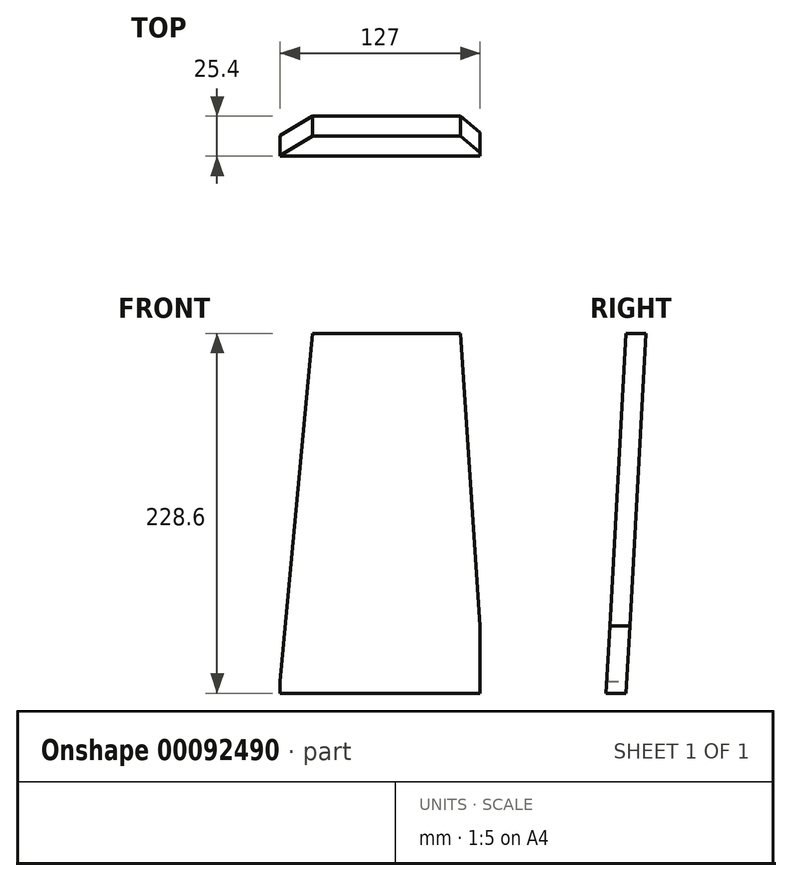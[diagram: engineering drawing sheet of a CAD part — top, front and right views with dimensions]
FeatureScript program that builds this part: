
annotation { "Feature Type Name" : "Feature", "Feature Type Description" : "" }
export const myFeature = defineFeature(function(context is Context, id is Id, definition is map)
    precondition{}
    {
        {
            var Q0;
            Q0=qCreatedBy(makeId("Top.planeOp"),FACE);
            var sketch = newSketch(context, id + "F0", { "sketchPlane" : qUnion([Q0])});
            skLineSegment(sketch, "E0.bottom", {"start": v(63.5, 6.35) * mm, "end": v(-63.5, 6.35) * mm});
            skLineSegment(sketch, "E0.top", {"start": v(63.5, -6.35) * mm, "end": v(-63.5, -6.35) * mm});
            skLineSegment(sketch, "E0.left", {"start": v(63.5, 6.35) * mm, "end": v(63.5, -6.35) * mm});
            skLineSegment(sketch, "E0.right", {"start": v(-63.5, 6.35) * mm, "end": v(-63.5, -6.35) * mm});
            skPoint(sketch, "E0.middle", {"position": v(0, 0) * mm});
            skSolve(sketch);
        }
        {
            var Q0;
            Q0=qCreatedBy(makeId("Top.planeOp"),FACE);
            cPlane(context, id + "F1", {"entities" : qUnion([Q0]), "cplaneType" : CPlaneType.OFFSET, "offset" : 228.6 * mm, "width" : 152.4 * mm, "height" : 152.4 * mm});
        }
        {
            var Q0;
            Q0=qCreatedBy(id+"F1.planeOp",FACE);
            var sketch = newSketch(context, id + "F2", { "sketchPlane" : qUnion([Q0])});
            skLineSegment(sketch, "E1", {"start": v(0, 0) * mm, "end": v(0, 12.7) * mm, "construction": true});
            skLineSegment(sketch, "E2", {"start": v(0, 12.7) * mm, "end": v(6.35, 12.7) * mm, "construction": true});
            skLineSegment(sketch, "E3.bottom", {"start": v(53.98, 16.51) * mm, "end": v(-41.28, 16.51) * mm});
            skLineSegment(sketch, "E3.top", {"start": v(53.98, 8.9) * mm, "end": v(-41.28, 8.89) * mm});
            skLineSegment(sketch, "E3.left", {"start": v(53.98, 16.51) * mm, "end": v(53.98, 8.9) * mm, "construction": true});
            skLineSegment(sketch, "E3.right", {"start": v(-41.28, 16.51) * mm, "end": v(-41.28, 8.89) * mm, "construction": true});
            skPoint(sketch, "E3.middle", {"position": v(6.35, 12.7) * mm});
            skSolve(sketch);
        }
        {
            var Q0;
            Q0=qCreatedBy(makeId("Right.planeOp"),FACE);
            var sketch = newSketch(context, id + "F3", { "sketchPlane" : qUnion([Q0])});
            skLineSegment(sketch, "E4", {"start": v(0, 0) * mm, "end": v(0, 228.6) * mm, "construction": true});
            skLineSegment(sketch, "E5", {"start": v(0, 228.6) * mm, "end": v(12.7, 228.6) * mm, "construction": true});
            skLineSegment(sketch, "E6", {"start": v(0, 114.3) * mm, "end": v(6.35, 114.3) * mm, "construction": true});
            skFitSpline(sketch, "E7", {"points": [v(0, 0) * mm, v(6.35, 114.3) * mm, v(12.7, 228.6) * mm], "startDerivative": vector(12.7, 228.6) * mm, "endDerivative": vector(12.7, 228.6) * mm});
            skSolve(sketch);
        }
        {
            var Q0;
            Q0 = qSketchRegion(id + "F0", true);
            var Q1;
            Q1 = qSketchRegion(id + "F2", true);
            var Q2;
            Q2 = qConstructionFilter(qBodyType(qCreatedBy(id + "F3" ,EDGE), BodyType.WIRE), ConstructionObject.NO);
            sweep(context, id + "F4", {"profiles" : qUnion([Q0, Q1]), "path" : qUnion([Q2])});
        }
        {
            var Q0;
            Q0=qCreatedBy(makeId("Front.planeOp"),FACE);
            var sketch = newSketch(context, id + "F5", { "sketchPlane" : qUnion([Q0])});
            skLineSegment(sketch, "E8", {"start": v(-41.9, 241.15) * mm, "end": v(-68.56, -47.21) * mm});
            skLineSegment(sketch, "E9", {"start": v(-68.56, -47.21) * mm, "end": v(-112.3, -35.6) * mm});
            skLineSegment(sketch, "E10", {"start": v(-112.3, -35.6) * mm, "end": v(-71.3, 241.15) * mm});
            skLineSegment(sketch, "E11", {"start": v(-71.3, 241.15) * mm, "end": v(-41.9, 241.15) * mm});
            skLineSegment(sketch, "E12", {"start": v(50.34, 239.1) * mm, "end": v(68.8, -36.28) * mm});
            skLineSegment(sketch, "E13", {"start": v(68.8, -36.28) * mm, "end": v(105.7, -28.08) * mm});
            skLineSegment(sketch, "E14", {"start": v(105.7, -28.08) * mm, "end": v(71.52, 243.2) * mm});
            skLineSegment(sketch, "E15", {"start": v(71.52, 243.2) * mm, "end": v(50.34, 239.1) * mm});
            skSolve(sketch);
        }
        {
            var Q0;
            Q0=makeQuery(id+"F5.imprint","IMPRINT",FACE,{"disambiguationData":[TD([[makeQuery(id+"F5.imprint","IMPRINT",EDGE,{"derivedFrom":sQuery(id+"F5.wireOp",EDGE,"E8")}),-1.0]])]});
            var Q1;
            Q1=makeQuery(id+"F5.imprint","IMPRINT",FACE,{"disambiguationData":[TD([[makeQuery(id+"F5.imprint","IMPRINT",EDGE,{"derivedFrom":sQuery(id+"F5.wireOp",EDGE,"E12")}),1.0]])]});
            extrude(context, id + "F6", {"entities" : qUnion([Q0, Q1]), "operationType" : NewBodyOperationType.REMOVE, "endBound" : BoundingType.SYMMETRIC, "oppositeDirection" : true, "depth" : 50.8 * mm});
        }
    });
